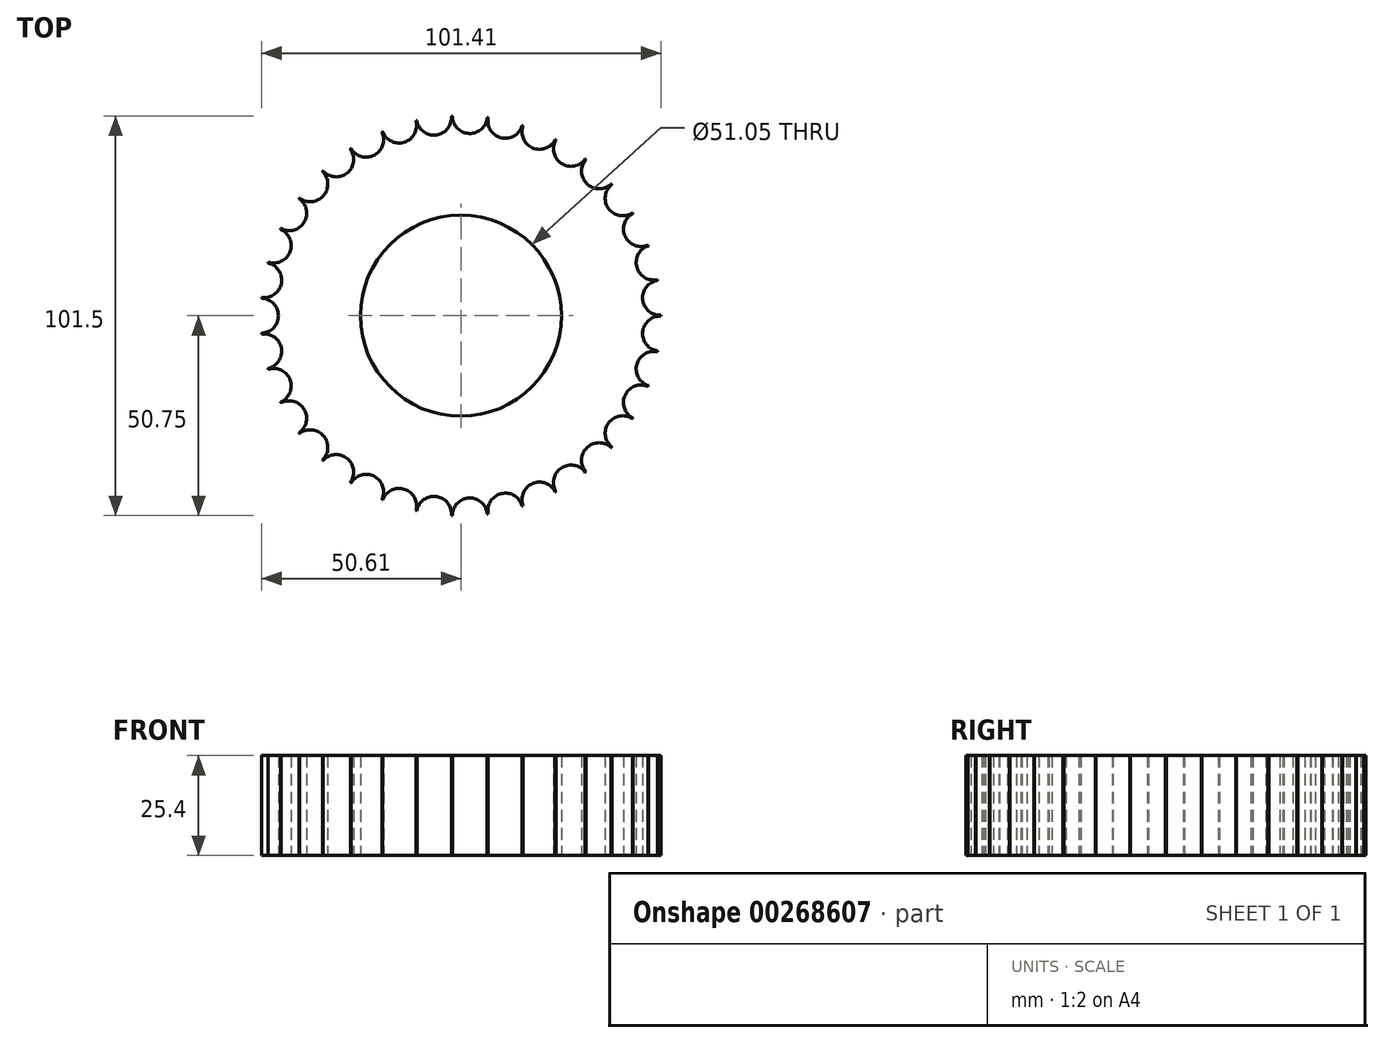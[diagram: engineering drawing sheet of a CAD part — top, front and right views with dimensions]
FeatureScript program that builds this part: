
annotation { "Feature Type Name" : "Feature", "Feature Type Description" : "" }
export const myFeature = defineFeature(function(context is Context, id is Id, definition is map)
    precondition{}
    {
        {
            var Q0;
            Q0=qCreatedBy(makeId("Top.planeOp"),FACE);
            var sketch = newSketch(context, id + "F0", { "sketchPlane" : qUnion([Q0])});
            skCircle(sketch, "E0", {"center": v(0, 0) * mm, "radius": 25.53 * mm});
            skCircle(sketch, "E1", {"center": v(0, 0) * mm, "radius": 50.8 * mm});
            skCircle(sketch, "E2", {"center": v(-50.8, 0) * mm, "radius": 4.45 * mm});
            skCircle(sketch, "E3.1.0", {"center": v(-49.98, -9.07) * mm, "radius": 4.45 * mm});
            skCircle(sketch, "E3.2.0", {"center": v(-47.56, -17.85) * mm, "radius": 4.45 * mm});
            skCircle(sketch, "E3.3.0", {"center": v(-43.6, -26.06) * mm, "radius": 4.45 * mm});
            skCircle(sketch, "E3.4.0", {"center": v(-38.26, -33.42) * mm, "radius": 4.45 * mm});
            skCircle(sketch, "E3.5.0", {"center": v(-31.67, -39.72) * mm, "radius": 4.45 * mm});
            skCircle(sketch, "E3.6.0", {"center": v(-24.07, -44.73) * mm, "radius": 4.45 * mm});
            skCircle(sketch, "E3.7.0", {"center": v(-15.7, -48.31) * mm, "radius": 4.45 * mm});
            skCircle(sketch, "E3.8.0", {"center": v(-6.82, -50.34) * mm, "radius": 4.45 * mm});
            skCircle(sketch, "E3.9.0", {"center": v(2.28, -50.75) * mm, "radius": 4.45 * mm});
            skCircle(sketch, "E3.10.0", {"center": v(11.3, -49.53) * mm, "radius": 4.45 * mm});
            skCircle(sketch, "E3.11.0", {"center": v(19.97, -46.71) * mm, "radius": 4.45 * mm});
            skCircle(sketch, "E3.12.0", {"center": v(27.99, -42.4) * mm, "radius": 4.45 * mm});
            skCircle(sketch, "E3.13.0", {"center": v(35.1, -36.72) * mm, "radius": 4.45 * mm});
            skCircle(sketch, "E3.14.0", {"center": v(41.1, -29.86) * mm, "radius": 4.45 * mm});
            skCircle(sketch, "E3.15.0", {"center": v(45.77, -22.04) * mm, "radius": 4.45 * mm});
            skCircle(sketch, "E3.16.0", {"center": v(48.97, -13.51) * mm, "radius": 4.45 * mm});
            skCircle(sketch, "E3.17.0", {"center": v(50.6, -4.55) * mm, "radius": 4.45 * mm});
            skCircle(sketch, "E3.18.0", {"center": v(50.6, 4.55) * mm, "radius": 4.45 * mm});
            skCircle(sketch, "E3.19.0", {"center": v(48.97, 13.51) * mm, "radius": 4.45 * mm});
            skCircle(sketch, "E3.20.0", {"center": v(45.77, 22.04) * mm, "radius": 4.45 * mm});
            skCircle(sketch, "E3.21.0", {"center": v(41.1, 29.86) * mm, "radius": 4.45 * mm});
            skCircle(sketch, "E3.22.0", {"center": v(35.1, 36.72) * mm, "radius": 4.45 * mm});
            skCircle(sketch, "E3.23.0", {"center": v(27.99, 42.4) * mm, "radius": 4.45 * mm});
            skCircle(sketch, "E3.24.0", {"center": v(19.97, 46.71) * mm, "radius": 4.45 * mm});
            skCircle(sketch, "E3.25.0", {"center": v(11.3, 49.53) * mm, "radius": 4.45 * mm});
            skCircle(sketch, "E3.26.0", {"center": v(2.28, 50.75) * mm, "radius": 4.44 * mm});
            skCircle(sketch, "E3.27.0", {"center": v(-6.82, 50.34) * mm, "radius": 4.45 * mm});
            skCircle(sketch, "E3.28.0", {"center": v(-15.7, 48.31) * mm, "radius": 4.45 * mm});
            skCircle(sketch, "E3.29.0", {"center": v(-24.07, 44.73) * mm, "radius": 4.45 * mm});
            skCircle(sketch, "E3.30.0", {"center": v(-31.67, 39.72) * mm, "radius": 4.45 * mm});
            skCircle(sketch, "E3.31.0", {"center": v(-38.26, 33.42) * mm, "radius": 4.45 * mm});
            skCircle(sketch, "E3.32.0", {"center": v(-43.6, 26.06) * mm, "radius": 4.45 * mm});
            skCircle(sketch, "E3.33.0", {"center": v(-47.56, 17.85) * mm, "radius": 4.45 * mm});
            skCircle(sketch, "E3.34.0", {"center": v(-49.98, 9.07) * mm, "radius": 4.45 * mm});
            skSolve(sketch);
        }
        {
            var Q0;
            Q0=makeQuery(id+"F0.imprint","IMPRINT",FACE,{"disambiguationData":[TD([[makeQuery(id+"F0.imprint","IMPRINT",EDGE,{"derivedFrom":sQuery(id+"F0.wireOp",EDGE,"E0")}),-1.0]])]});
            extrude(context, id + "F1", {"entities" : qUnion([Q0]), "depth" : 25.4 * mm});
        }
    });
